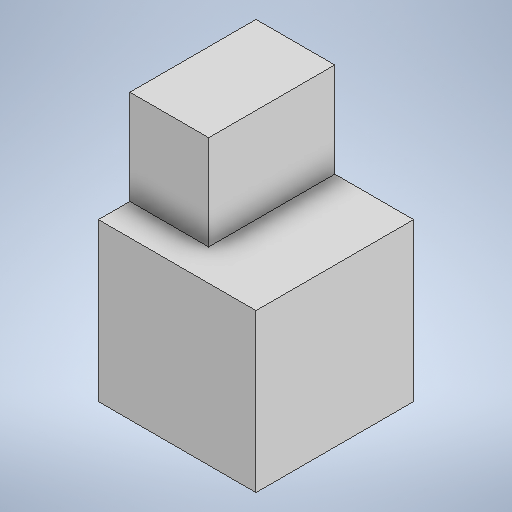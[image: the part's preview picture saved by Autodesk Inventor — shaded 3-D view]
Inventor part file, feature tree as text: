
AUTODESK INVENTOR PART (.ipt)
format: ipt  version: 2025 (Build 290162000, 162)  size: 222,208 bytes
history: native  units: mm
features: extrude x3, sketch x3, projected_geometry x2
ambient origin geometry x8: Origin, YZ Plane, XZ Plane, XY Plane, X Axis, Y Axis, Z Axis, Center Point
bodies: Solid1 (feature_tree), Solid2 (feature_tree)
feature tree (8):
  extrude  "Extrusion1"  Depth=10.0mm
  extrude  "Extrusion2"  Depth=5.0mm
  extrude  "Extrusion3"  Depth=4.0mm TaperAngle=0.0deg
  sketch  "Sketch1"  dims[d0=10.0mm d1=10.0mm]
  sketch  "Sketch2"  dims[d2=10.0mm d3=0.0mm d4=5.0mm]
  projected_geometry  "Projected Loop1"
  sketch  "Sketch3"  dims[d5=8.0mm d6=4.0mm d7=0.0mm d8=10.0mm d9=0.0mm]
  projected_geometry  "Projected Loop2"
